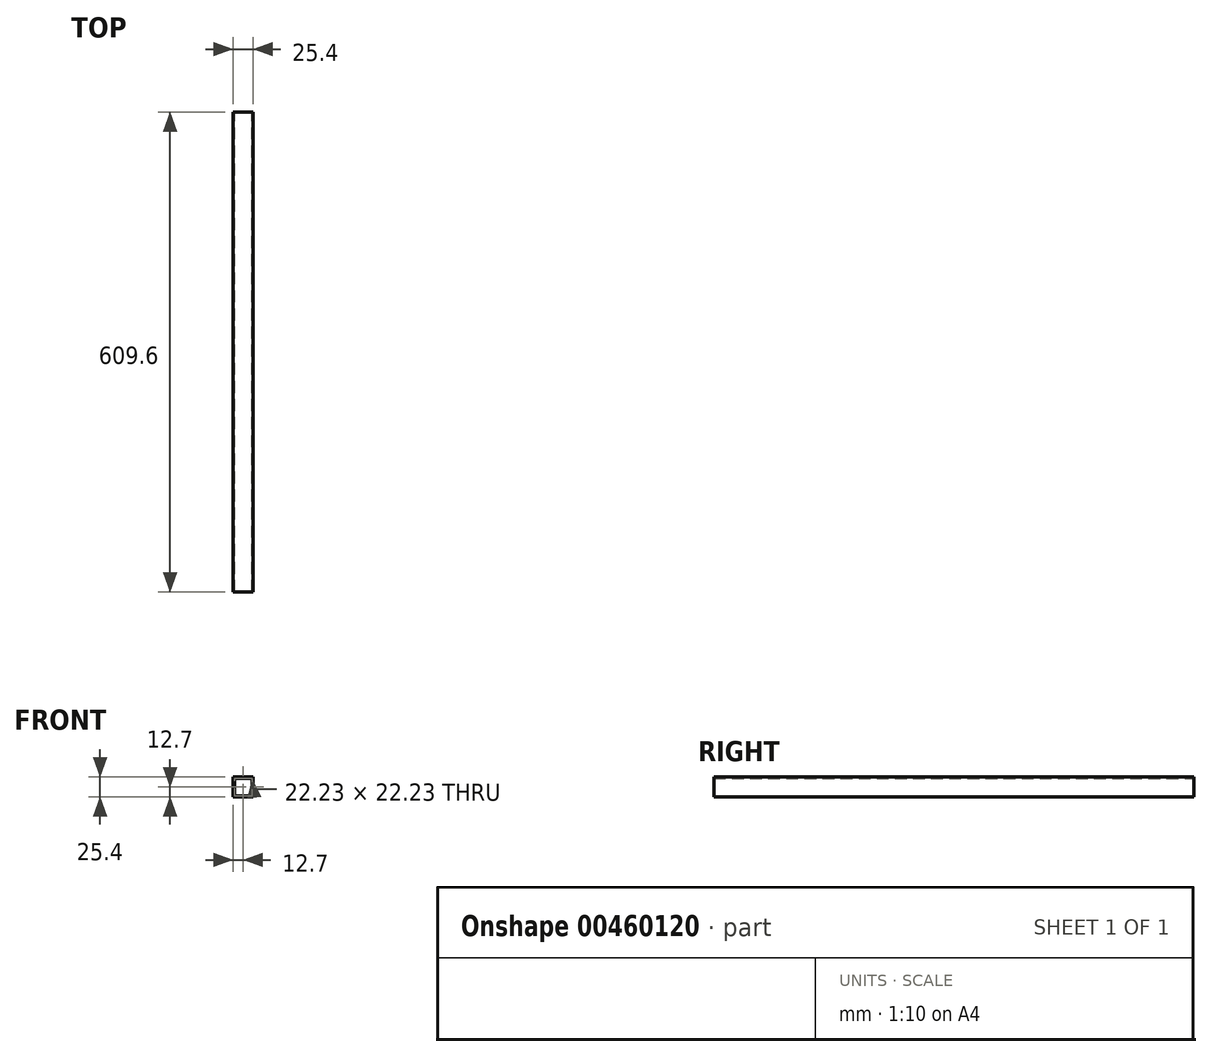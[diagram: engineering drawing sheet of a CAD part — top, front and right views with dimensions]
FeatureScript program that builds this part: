
annotation { "Feature Type Name" : "Feature", "Feature Type Description" : "" }
export const myFeature = defineFeature(function(context is Context, id is Id, definition is map)
    precondition{}
    {
        {
            var Q0;
            Q0=qCreatedBy(makeId("Front.planeOp"),FACE);
            var sketch = newSketch(context, id + "F0", { "sketchPlane" : qUnion([Q0])});
            skLineSegment(sketch, "E0.bottom", {"start": v(12.7, 12.7) * mm, "end": v(-12.7, 12.7) * mm});
            skLineSegment(sketch, "E0.top", {"start": v(12.7, -12.7) * mm, "end": v(-12.7, -12.7) * mm});
            skLineSegment(sketch, "E0.left", {"start": v(12.7, 12.7) * mm, "end": v(12.7, -12.7) * mm});
            skLineSegment(sketch, "E0.right", {"start": v(-12.7, 12.7) * mm, "end": v(-12.7, -12.7) * mm});
            skPoint(sketch, "E0.middle", {"position": v(0, 0) * mm});
            skLineSegment(sketch, "E1.bottom", {"start": v(11.11, 11.11) * mm, "end": v(-11.11, 11.11) * mm});
            skLineSegment(sketch, "E1.top", {"start": v(11.11, -11.11) * mm, "end": v(-11.11, -11.11) * mm});
            skLineSegment(sketch, "E1.left", {"start": v(11.11, 11.11) * mm, "end": v(11.11, -11.11) * mm});
            skLineSegment(sketch, "E1.right", {"start": v(-11.11, 11.11) * mm, "end": v(-11.11, -11.11) * mm});
            skSolve(sketch);
        }
        {
            var Q0;
            Q0=makeQuery(id+"F0.imprint","IMPRINT",FACE,{"disambiguationData":[TD([[makeQuery(id+"F0.imprint","IMPRINT",EDGE,{"derivedFrom":sQuery(id+"F0.wireOp",EDGE,"E0.bottom")}),1.0]])]});
            extrude(context, id + "F1", {"entities" : qUnion([Q0]), "depth" : 609.6 * mm});
        }
    });
